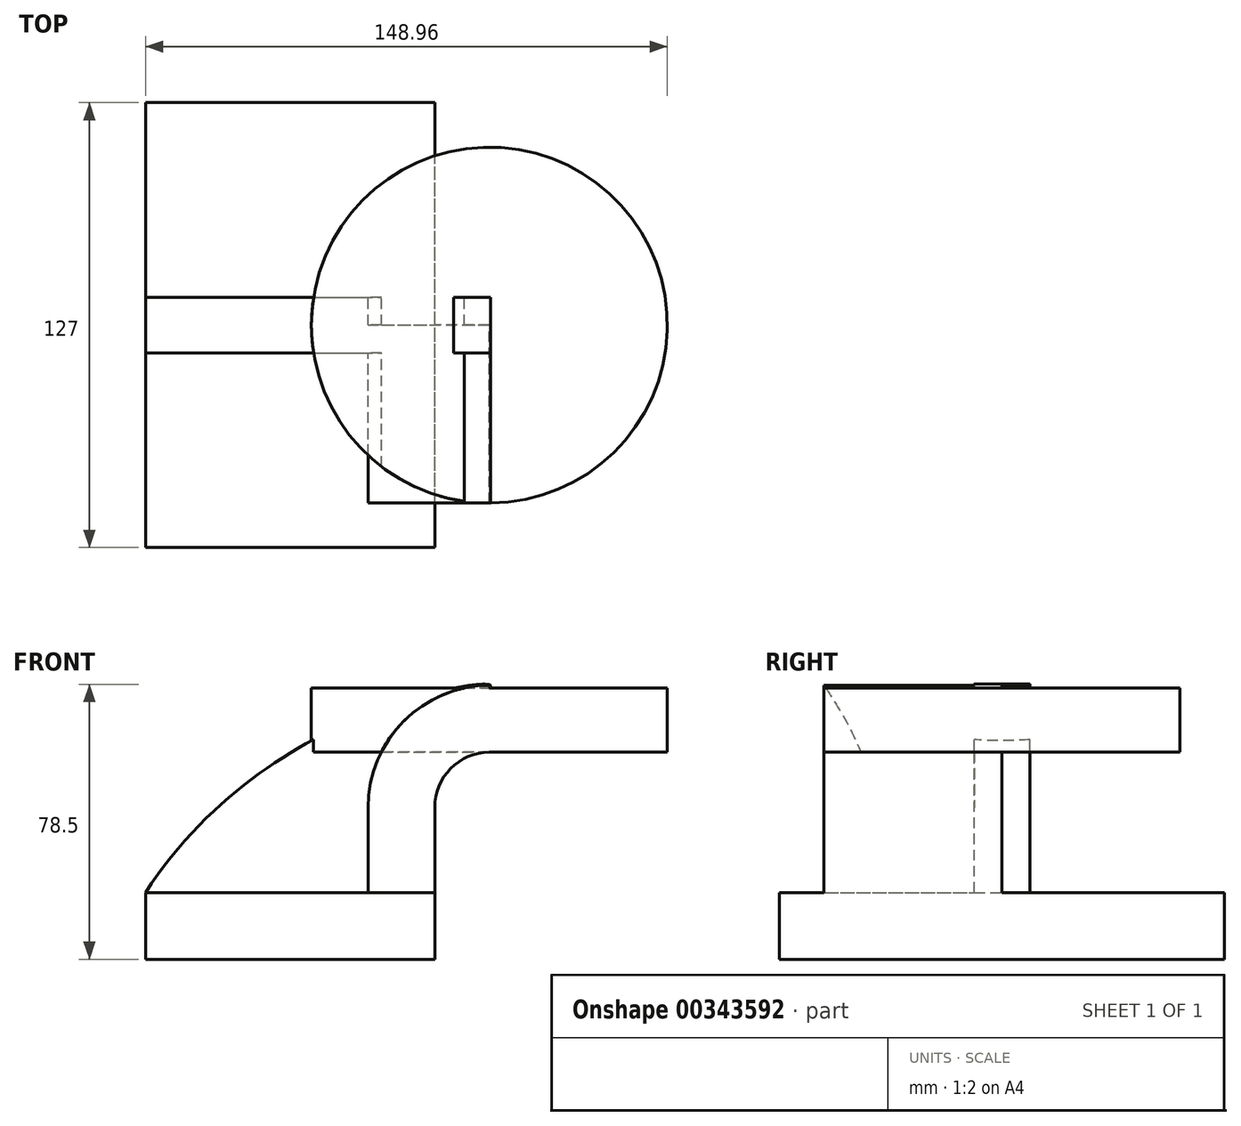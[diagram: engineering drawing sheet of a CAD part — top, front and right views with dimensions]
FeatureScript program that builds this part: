
annotation { "Feature Type Name" : "Feature", "Feature Type Description" : "" }
export const myFeature = defineFeature(function(context is Context, id is Id, definition is map)
    precondition{}
    {
        {
            var Q0;
            Q0=qCreatedBy(makeId("Front.planeOp"),FACE);
            var sketch = newSketch(context, id + "F0", { "sketchPlane" : qUnion([Q0])});
            skLineSegment(sketch, "E0.bottom", {"start": v(-41.28, 9.52) * mm, "end": v(41.27, 9.53) * mm});
            skLineSegment(sketch, "E0.top", {"start": v(-41.28, -9.53) * mm, "end": v(41.28, -9.53) * mm});
            skLineSegment(sketch, "E0.left", {"start": v(-41.28, 9.52) * mm, "end": v(-41.27, -9.53) * mm});
            skLineSegment(sketch, "E0.right", {"start": v(41.28, 9.53) * mm, "end": v(41.28, -9.52) * mm});
            skPoint(sketch, "E0.middle", {"position": v(0, 0) * mm});
            skLineSegment(sketch, "E1.bottom", {"start": v(56.88, 67.9) * mm, "end": v(107.68, 67.9) * mm});
            skLineSegment(sketch, "E1.top", {"start": v(56.88, 39.32) * mm, "end": v(107.68, 39.32) * mm});
            skLineSegment(sketch, "E1.left", {"start": v(56.88, 67.9) * mm, "end": v(56.88, 39.32) * mm});
            skLineSegment(sketch, "E1.right", {"start": v(107.68, 67.9) * mm, "end": v(107.68, 39.32) * mm});
            skPoint(sketch, "E1.middle", {"position": v(82.28, 53.6) * mm});
            skLineSegment(sketch, "E2", {"start": v(41.27, 9.53) * mm, "end": v(41.27, 33.76) * mm});
            skArc(sketch, "E3", {"start": v(41.27, 33.76) * mm, "mid": v(45.92, 44.99) * mm, "end": v(57.15, 49.64) * mm});
            skLineSegment(sketch, "E4", {"start": v(57.15, 49.64) * mm, "end": v(109.55, 49.64) * mm});
            skArc(sketch, "E5.0", {"start": v(22.22, 33.76) * mm, "mid": v(32.45, 58.46) * mm, "end": v(57.15, 68.69) * mm});
            skLineSegment(sketch, "E5.1", {"start": v(22.22, 9.53) * mm, "end": v(22.22, 33.76) * mm});
            skLineSegment(sketch, "E6", {"start": v(57.15, 49.64) * mm, "end": v(56.88, 67.9) * mm});
            skLineSegment(sketch, "E7", {"start": v(41.28, 9.53) * mm, "end": v(22.22, 9.53) * mm});
            skFitSpline(sketch, "E8", {"points": [v(-41.28, 9.52) * mm, v(57.15, 68.69) * mm, v(56.88, 67.9) * mm], "startDerivative": vector(109.68, 169.84) * mm, "endDerivative": vector(-7.83, -12.98) * mm});
            skSolve(sketch);
        }
        {
            var Q0;
            Q0=makeQuery(id+"F0.imprint","IMPRINT",FACE,{"disambiguationData":[TD([[makeQuery(id+"F0.imprint","IMPRINT",EDGE,{"derivedFrom":sQuery(id+"F0.wireOp",EDGE,"E0.bottom")}),-1.0]])]});
            extrude(context, id + "F1", {"entities" : qUnion([Q0]), "endBound" : BoundingType.SYMMETRIC, "depth" : 127 * mm});
        }
        {
            var Q0;
            {var subQ1=sQuery(id+"F0.wireOp",EDGE,"E2");Q0=makeQuery(id+"F0.imprint","IMPRINT",FACE,{"disambiguationData":[TD([[makeQuery(id+"F0.imprint","IMPRINT",EDGE,{"derivedFrom":subQ1}),1.0]])]});}
            extrude(context, id + "F2", {"entities" : qUnion([Q0]), "operationType" : NewBodyOperationType.ADD, "depth" : 50.8 * mm});
        }
        {
            var Q0;
            {var subQ0=sQuery(id+"F0.wireOp",EDGE,"E0.bottom");Q0=makeQuery(id+"F0.imprint","IMPRINT",FACE,{"disambiguationData":[TD([[makeQuery(id+"F0.imprint","IMPRINT",EDGE,{"derivedFrom":subQ0}),1.0]])]});}
            extrude(context, id + "F3", {"entities" : qUnion([Q0]), "operationType" : NewBodyOperationType.ADD, "endBound" : BoundingType.SYMMETRIC, "depth" : 15.88 * mm});
        }
        {
            var Q0;
            Q0=makeQuery(id+"F2.opExtrude","SWEPT_FACE",FACE,{"disambiguationData":[OSD([sQuery(id+"F0.wireOp",EDGE,"E1.left")])]});
            var Q1;
            Q1=makeQuery(id+"F2.opExtrude","CAP_EDGE",EDGE,{"disambiguationData":[OSD([sQuery(id+"F0.wireOp",EDGE,"E1.left")])],"isStart":true});
            revolve(context, id + "F4", {"operationType" : NewBodyOperationType.ADD, "entities" : qUnion([Q0]), "axis" : qUnion([Q1]), "revolveType" : RevolveType.FULL});
        }
    });
